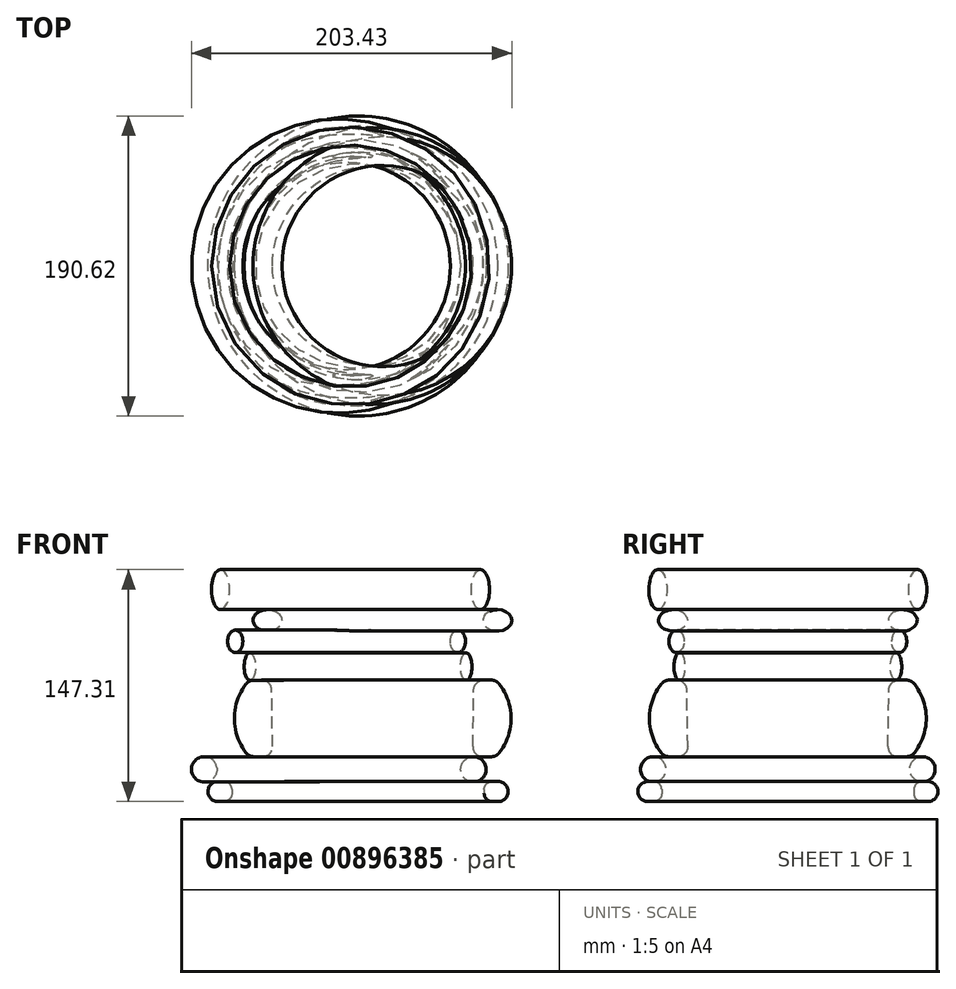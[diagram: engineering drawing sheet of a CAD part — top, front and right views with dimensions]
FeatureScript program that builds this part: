
annotation { "Feature Type Name" : "Feature", "Feature Type Description" : "" }
export const myFeature = defineFeature(function(context is Context, id is Id, definition is map)
    precondition{}
    {
        {
            var Q0;
            Q0=qCreatedBy(makeId("Front.planeOp"),FACE);
            var sketch = newSketch(context, id + "F0", { "sketchPlane" : qUnion([Q0])});
            skArc(sketch, "E0", {"start": v(88.88, 0.73) * mm, "mid": v(95.3, 7.04) * mm, "end": v(88.96, 13.43) * mm});
            skLineSegment(sketch, "E1", {"start": v(0, 12.7) * mm, "end": v(0, 0) * mm, "construction": true});
            skLineSegment(sketch, "E2", {"start": v(88.96, 13.43) * mm, "end": v(80.08, 13.43) * mm});
            skLineSegment(sketch, "E3", {"start": v(80.08, 13.43) * mm, "end": v(80.1, 0.73) * mm});
            skLineSegment(sketch, "E4", {"start": v(80.1, 0.73) * mm, "end": v(88.88, 0.73) * mm});
            skSolve(sketch);
        }
        {
            var Q0;
            Q0=makeQuery(id+"F0.imprint","IMPRINT",FACE,{"disambiguationData":[TD([[makeQuery(id+"F0.imprint","IMPRINT",EDGE,{"derivedFrom":sQuery(id+"F0.wireOp",EDGE,"E0")}),1.0]])]});
            var Q1;
            Q1=sQuery(id+"F0.wireOp",EDGE,"E1");
            revolve(context, id + "F1", {"surfaceOperationType" : NewSurfaceOperationType.NEW, "entities" : qUnion([Q0]), "axis" : qUnion([Q1]), "revolveType" : RevolveType.FULL});
        }
        {
            var Q0;
            Q0=makeQuery(id+"F1.opRevolve","SWEPT_EDGE",EDGE,{"disambiguationData":[OSD([sQuery(id+"F0.wireOp",EDGE,"E2"),sQuery(id+"F0.wireOp",EDGE,"E3")])]});
            var Q1;
            Q1=makeQuery(id+"F1.opRevolve","SWEPT_EDGE",EDGE,{"disambiguationData":[OSD([sQuery(id+"F0.wireOp",EDGE,"E3"),sQuery(id+"F0.wireOp",EDGE,"E4")])]});
            fillet(context, id + "F2", {"entities" : qUnion([Q0, Q1]), "radius" : 5.08 * mm, "tangentPropagation" : true, "allowEdgeOverflow" : false});
        }
        {
            var Q0;
            Q0=qCreatedBy(makeId("Front.planeOp"),FACE);
            var sketch = newSketch(context, id + "F3", { "sketchPlane" : qUnion([Q0])});
            skLineSegment(sketch, "E5", {"start": v(-12.23, 14.25) * mm, "end": v(-12.23, 29.21) * mm, "construction": true});
            skLineSegment(sketch, "E6", {"start": v(-12.23, 29.21) * mm, "end": v(-97.71, 29.21) * mm, "construction": true});
            skArc(sketch, "E7", {"start": v(-97.71, 29.21) * mm, "mid": v(-105.77, 21.15) * mm, "end": v(-97.71, 13.1) * mm});
            skArc(sketch, "E8", {"start": v(-97.71, 13.1) * mm, "mid": v(-89.65, 21.15) * mm, "end": v(-97.71, 29.21) * mm});
            skSolve(sketch);
        }
        {
            var Q0;
            Q0=makeQuery(id+"F3.imprint","IMPRINT",FACE,{"disambiguationData":[TD([[makeQuery(id+"F3.imprint","IMPRINT",EDGE,{"derivedFrom":sQuery(id+"F3.wireOp",EDGE,"E7")}),1.0]])]});
            var Q1;
            Q1=sQuery(id+"F3.wireOp",EDGE,"E5");
            revolve(context, id + "F4", {"operationType" : NewBodyOperationType.ADD, "surfaceOperationType" : NewSurfaceOperationType.NEW, "entities" : qUnion([Q0]), "axis" : qUnion([Q1]), "revolveType" : RevolveType.FULL});
        }
        {
            var Q0;
            Q0=qCreatedBy(makeId("Front.planeOp"),FACE);
            var sketch = newSketch(context, id + "F5", { "sketchPlane" : qUnion([Q0])});
            skLineSegment(sketch, "E9", {"start": v(9.3, 29.2) * mm, "end": v(9.3, 77.85) * mm, "construction": true});
            skLineSegment(sketch, "E10", {"start": v(79.8, 77.85) * mm, "end": v(84.63, 77.85) * mm});
            skArc(sketch, "E11", {"start": v(89.62, 31.62) * mm, "mid": v(97.2, 53.52) * mm, "end": v(89.62, 75.43) * mm});
            skLineSegment(sketch, "E12", {"start": v(84.63, 29.2) * mm, "end": v(79.24, 29.2) * mm});
            skLineSegment(sketch, "E13", {"start": v(72.9, 35.64) * mm, "end": v(73.45, 71.6) * mm});
            skPoint(sketch, "E14.visualSharp", {"position": v(87.53, 77.85) * mm});
            skArc(sketch, "E14.filletArc", {"start": v(89.62, 75.43) * mm, "mid": v(87.4, 77.21) * mm, "end": v(84.63, 77.85) * mm});
            skPoint(sketch, "E15.visualSharp", {"position": v(87.53, 29.2) * mm});
            skArc(sketch, "E15.filletArc", {"start": v(84.63, 29.2) * mm, "mid": v(87.4, 29.83) * mm, "end": v(89.62, 31.62) * mm});
            skPoint(sketch, "E16.visualSharp", {"position": v(72.8, 29.2) * mm});
            skArc(sketch, "E16.filletArc", {"start": v(72.9, 35.64) * mm, "mid": v(74.72, 31.09) * mm, "end": v(79.24, 29.2) * mm});
            skPoint(sketch, "E17.visualSharp", {"position": v(73.55, 77.85) * mm});
            skArc(sketch, "E17.filletArc", {"start": v(79.8, 77.85) * mm, "mid": v(75.35, 76.03) * mm, "end": v(73.45, 71.6) * mm});
            skSolve(sketch);
        }
        {
            var Q0;
            Q0=makeQuery(id+"F5.imprint","IMPRINT",FACE,{"disambiguationData":[TD([[makeQuery(id+"F5.imprint","IMPRINT",EDGE,{"derivedFrom":sQuery(id+"F5.wireOp",EDGE,"E10")}),-1.0]])]});
            var Q1;
            Q1=sQuery(id+"F5.wireOp",EDGE,"E9");
            revolve(context, id + "F6", {"operationType" : NewBodyOperationType.ADD, "surfaceOperationType" : NewSurfaceOperationType.NEW, "entities" : qUnion([Q0]), "axis" : qUnion([Q1]), "revolveType" : RevolveType.FULL});
        }
        {
            var Q0;
            Q0=qCreatedBy(makeId("Front.planeOp"),FACE);
            var sketch = newSketch(context, id + "F7", { "sketchPlane" : qUnion([Q0])});
            skLineSegment(sketch, "E18", {"start": v(0, 77.62) * mm, "end": v(0, 95.17) * mm, "construction": true});
            skLineSegment(sketch, "E19", {"start": v(0, 95.17) * mm, "end": v(-68.74, 95.17) * mm, "construction": true});
            skLineSegment(sketch, "E20", {"start": v(-68.74, 95.17) * mm, "end": v(-68.74, 77.62) * mm, "construction": true});
            skLineSegment(sketch, "E21", {"start": v(-68.74, 77.62) * mm, "end": v(0, 77.62) * mm, "construction": true});
            skEllipse(sketch, "E22", {"center": v(-68.74, 86.4) * mm, "majorRadius": 8.77 * mm, "minorRadius": 3.61 * mm, "majorAxis": v(0, -1)});
            skSolve(sketch);
        }
        {
            var Q0;
            Q0=makeQuery(id+"F7.imprint","IMPRINT",FACE,{"disambiguationData":[TD([[makeQuery(id+"F7.imprint","IMPRINT",EDGE,{"derivedFrom":sQuery(id+"F7.wireOp",EDGE,"E22")}),1.0]])]});
            var Q1;
            Q1=sQuery(id+"F7.wireOp",EDGE,"E18");
            revolve(context, id + "F8", {"operationType" : NewBodyOperationType.ADD, "surfaceOperationType" : NewSurfaceOperationType.NEW, "entities" : qUnion([Q0]), "axis" : qUnion([Q1]), "revolveType" : RevolveType.FULL});
        }
        {
            var Q0;
            Q0=qCreatedBy(makeId("Front.planeOp"),FACE);
            var sketch = newSketch(context, id + "F9", { "sketchPlane" : qUnion([Q0])});
            skLineSegment(sketch, "E23", {"start": v(-7.28, 95.37) * mm, "end": v(-7.28, 109.6) * mm, "construction": true});
            skLineSegment(sketch, "E24", {"start": v(-7.28, 109.6) * mm, "end": v(-78, 109.6) * mm, "construction": true});
            skLineSegment(sketch, "E25", {"start": v(-78, 109.6) * mm, "end": v(-78, 95.37) * mm, "construction": true});
            skLineSegment(sketch, "E26", {"start": v(-78, 95.37) * mm, "end": v(-7.28, 95.37) * mm, "construction": true});
            skEllipse(sketch, "E27", {"center": v(-78, 102.48) * mm, "majorRadius": 7.11 * mm, "minorRadius": 4.8 * mm, "majorAxis": v(0, -1)});
            skSolve(sketch);
        }
        {
            var Q0;
            Q0=makeQuery(id+"F9.imprint","IMPRINT",FACE,{"disambiguationData":[TD([[makeQuery(id+"F9.imprint","IMPRINT",EDGE,{"derivedFrom":sQuery(id+"F9.wireOp",EDGE,"E27")}),1.0]])]});
            var Q1;
            Q1=sQuery(id+"F9.wireOp",EDGE,"E23");
            revolve(context, id + "F10", {"surfaceOperationType" : NewSurfaceOperationType.NEW, "entities" : qUnion([Q0]), "axis" : qUnion([Q1]), "revolveType" : RevolveType.FULL});
        }
        {
            var Q0;
            Q0=qCreatedBy(makeId("Front.planeOp"),FACE);
            var sketch = newSketch(context, id + "F11", { "sketchPlane" : qUnion([Q0])});
            skLineSegment(sketch, "E28", {"start": v(15.48, 109.03) * mm, "end": v(15.48, 122.58) * mm, "construction": true});
            skLineSegment(sketch, "E29", {"start": v(15.48, 122.58) * mm, "end": v(88.51, 122.58) * mm, "construction": true});
            skLineSegment(sketch, "E30", {"start": v(88.51, 122.58) * mm, "end": v(88.51, 109.03) * mm, "construction": true});
            skLineSegment(sketch, "E31", {"start": v(88.51, 109.03) * mm, "end": v(15.48, 109.03) * mm, "construction": true});
            skEllipse(sketch, "E32", {"center": v(88.51, 115.8) * mm, "majorRadius": 6.77 * mm, "minorRadius": 9.15 * mm, "majorAxis": v(0, -1)});
            skSolve(sketch);
        }
        {
            var Q0;
            Q0=makeQuery(id+"F11.imprint","IMPRINT",FACE,{"disambiguationData":[TD([[makeQuery(id+"F11.imprint","IMPRINT",EDGE,{"derivedFrom":sQuery(id+"F11.wireOp",EDGE,"E32")}),1.0]])]});
            var Q1;
            Q1=sQuery(id+"F11.wireOp",EDGE,"E28");
            revolve(context, id + "F12", {"operationType" : NewBodyOperationType.ADD, "surfaceOperationType" : NewSurfaceOperationType.NEW, "entities" : qUnion([Q0]), "axis" : qUnion([Q1]), "revolveType" : RevolveType.FULL});
        }
        {
            var Q0;
            Q0=qCreatedBy(makeId("Front.planeOp"),FACE);
            var sketch = newSketch(context, id + "F13", { "sketchPlane" : qUnion([Q0])});
            skLineSegment(sketch, "E33", {"start": v(-4.83, 122.64) * mm, "end": v(-4.83, 148.04) * mm, "construction": true});
            skLineSegment(sketch, "E34", {"start": v(-4.83, 148.04) * mm, "end": v(-87.38, 148.04) * mm, "construction": true});
            skLineSegment(sketch, "E35", {"start": v(-87.38, 148.04) * mm, "end": v(-87.38, 122.64) * mm, "construction": true});
            skLineSegment(sketch, "E36", {"start": v(-87.38, 122.64) * mm, "end": v(-4.83, 122.64) * mm, "construction": true});
            skEllipse(sketch, "E37", {"center": v(-87.38, 135.34) * mm, "majorRadius": 12.7 * mm, "minorRadius": 5.74 * mm, "majorAxis": v(0, -1)});
            skSolve(sketch);
        }
        {
            var Q0;
            Q0=makeQuery(id+"F13.imprint","IMPRINT",FACE,{"disambiguationData":[TD([[makeQuery(id+"F13.imprint","IMPRINT",EDGE,{"derivedFrom":sQuery(id+"F13.wireOp",EDGE,"E37")}),1.0]])]});
            var Q1;
            Q1=sQuery(id+"F13.wireOp",EDGE,"E33");
            revolve(context, id + "F14", {"surfaceOperationType" : NewSurfaceOperationType.NEW, "entities" : qUnion([Q0]), "axis" : qUnion([Q1]), "revolveType" : RevolveType.FULL});
        }
    });
